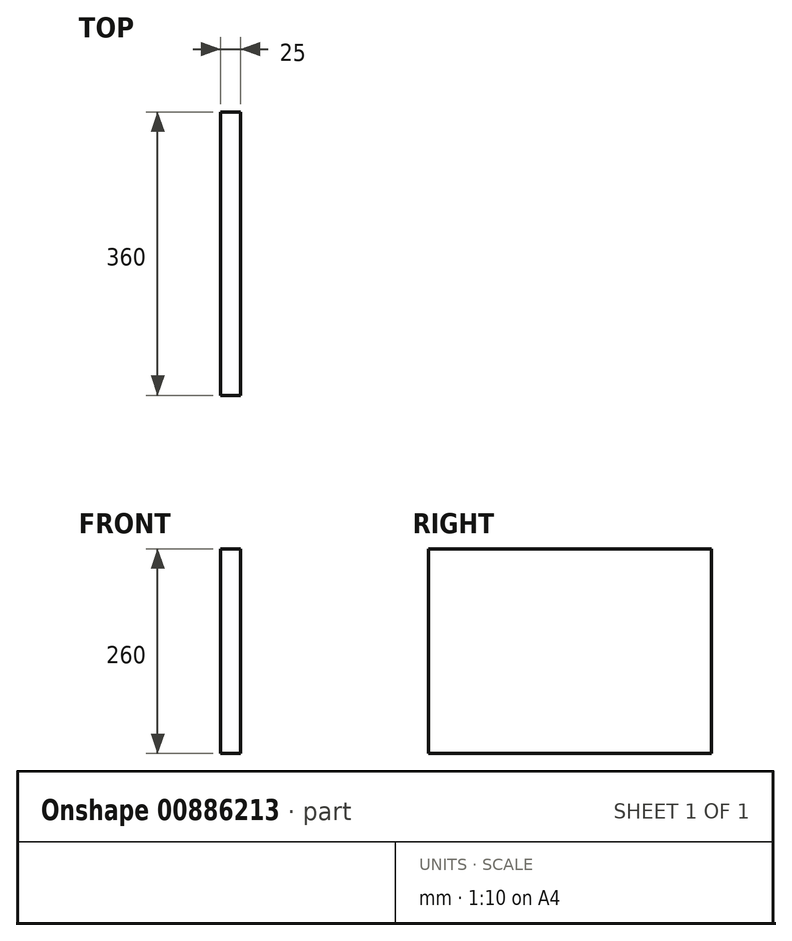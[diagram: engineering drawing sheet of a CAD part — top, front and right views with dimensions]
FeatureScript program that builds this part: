
annotation { "Feature Type Name" : "Feature", "Feature Type Description" : "" }
export const myFeature = defineFeature(function(context is Context, id is Id, definition is map)
    precondition{}
    {
        {
            var Q0;
            Q0=qCreatedBy(makeId("Right.planeOp"),FACE);
            var sketch = newSketch(context, id + "F0", { "sketchPlane" : qUnion([Q0])});
            skLineSegment(sketch, "E0.bottom", {"start": v(180, -130) * mm, "end": v(-180, -130) * mm});
            skLineSegment(sketch, "E0.top", {"start": v(180, 130) * mm, "end": v(-180, 130) * mm});
            skLineSegment(sketch, "E0.left", {"start": v(180, -130) * mm, "end": v(180, 130) * mm});
            skLineSegment(sketch, "E0.right", {"start": v(-180, -130) * mm, "end": v(-180, 130) * mm});
            skPoint(sketch, "E0.middle", {"position": v(0, 0) * mm});
            skSolve(sketch);
        }
        {
            var Q0;
            Q0 = qSketchRegion(id + "F0", true);
            extrude(context, id + "F1", {"entities" : qUnion([Q0]), "depth" : 25 * mm, "offsetDistance" : 25 * mm});
        }
    });
